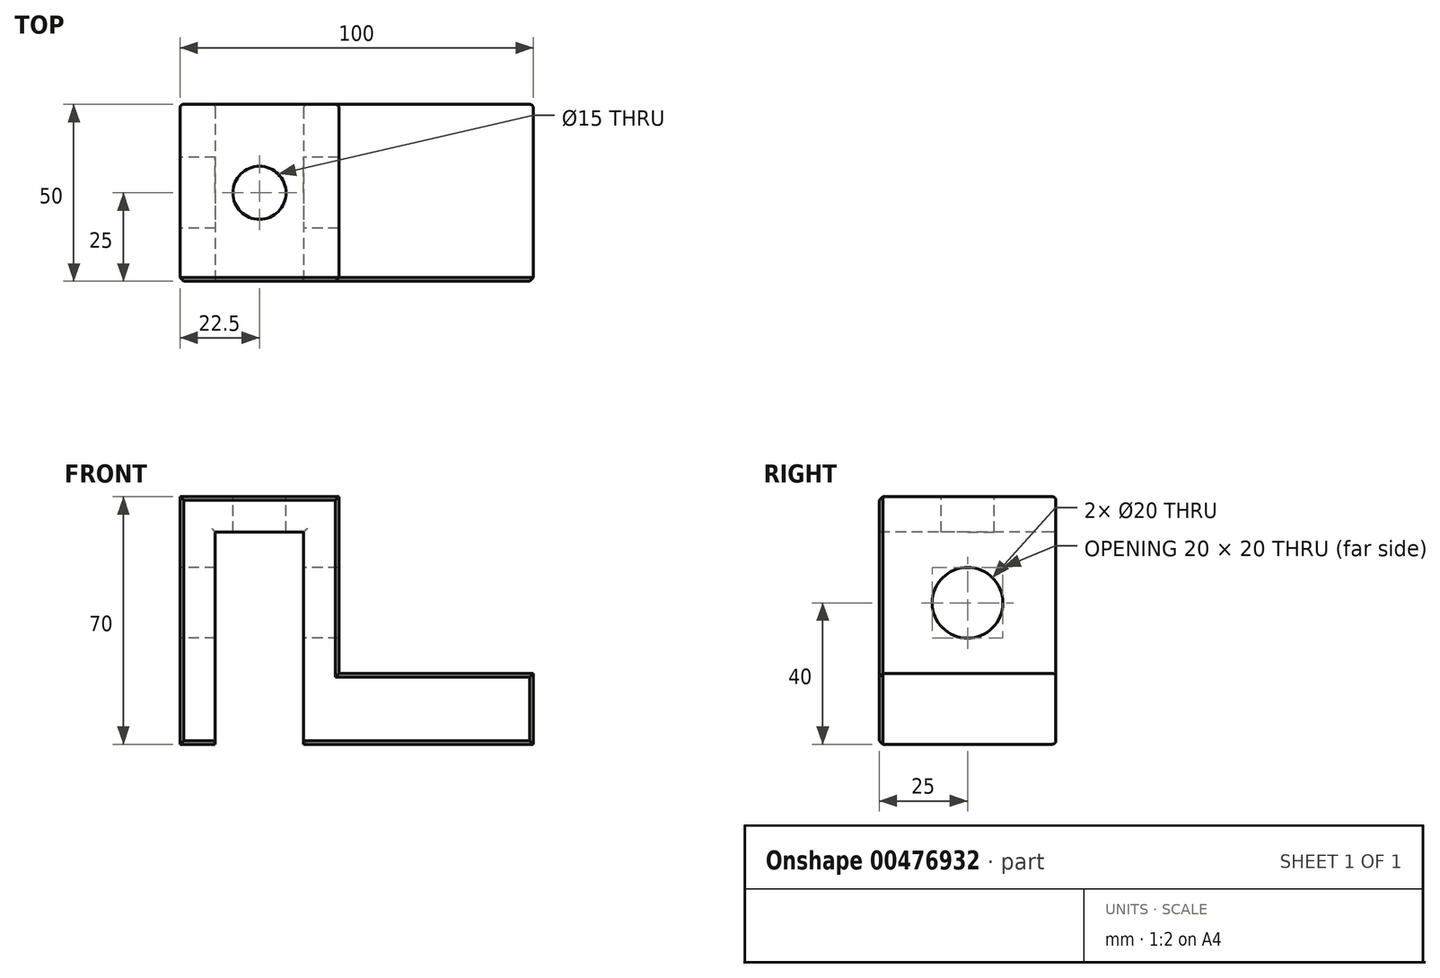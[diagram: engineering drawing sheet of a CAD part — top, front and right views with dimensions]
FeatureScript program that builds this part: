
annotation { "Feature Type Name" : "Feature", "Feature Type Description" : "" }
export const myFeature = defineFeature(function(context is Context, id is Id, definition is map)
    precondition{}
    {
        {
            var Q0;
            Q0=qCreatedBy(makeId("Top.planeOp"),FACE);
            var sketch = newSketch(context, id + "F0", { "sketchPlane" : qUnion([Q0])});
            skLineSegment(sketch, "E0.bottom", {"start": v(0, 0) * mm, "end": v(100, 0) * mm});
            skLineSegment(sketch, "E0.top", {"start": v(0, 50) * mm, "end": v(100, 50) * mm});
            skLineSegment(sketch, "E0.left", {"start": v(0, 0) * mm, "end": v(0, 50) * mm});
            skLineSegment(sketch, "E0.right", {"start": v(100, 0) * mm, "end": v(100, 50) * mm});
            skSolve(sketch);
        }
        {
            var Q0;
            Q0 = qSketchRegion(id + "F0", true);
            extrude(context, id + "F1", {"entities" : qUnion([Q0]), "depth" : 20 * mm});
        }
        {
            var Q0;
            Q0=makeQuery(id+"F1.opExtrude","CAP_FACE",FACE,{"disambiguationData":[OSD([sQuery(id+"F0.wireOp",EDGE,"E0.bottom"),sQuery(id+"F0.wireOp",EDGE,"E0.top"),sQuery(id+"F0.wireOp",EDGE,"E0.left"),sQuery(id+"F0.wireOp",EDGE,"E0.right")])],"isStart":false});
            var sketch = newSketch(context, id + "F2", { "sketchPlane" : qUnion([Q0])});
            skLineSegment(sketch, "E1.bottom", {"start": v(0, 0) * mm, "end": v(45, 0) * mm});
            skLineSegment(sketch, "E1.top", {"start": v(0, 50) * mm, "end": v(45, 50) * mm});
            skLineSegment(sketch, "E1.left", {"start": v(0, 0) * mm, "end": v(0, 50) * mm});
            skLineSegment(sketch, "E1.right", {"start": v(45, 0) * mm, "end": v(45, 50) * mm});
            skSolve(sketch);
        }
        {
            var Q0;
            Q0 = qSketchRegion(id + "F2", true);
            extrude(context, id + "F3", {"entities" : qUnion([Q0]), "operationType" : NewBodyOperationType.ADD, "depth" : 50 * mm});
        }
        {
            var Q0;
            Q0=makeQuery(id+"F3.boolean.opBoolean","MERGE",FACE,{"derivedFrom":[makeQuery(id+"F1.opExtrude","SWEPT_FACE",FACE,{"disambiguationData":[OSD([sQuery(id+"F0.wireOp",EDGE,"E0.bottom")])]}),makeQuery(id+"F3.opExtrude","SWEPT_FACE",FACE,{"disambiguationData":[OSD([sQuery(id+"F2.wireOp",EDGE,"E1.bottom")])]})]});
            var sketch = newSketch(context, id + "F4", { "sketchPlane" : qUnion([Q0])});
            skLineSegment(sketch, "E2.bottom", {"start": v(10, 0) * mm, "end": v(35, 0) * mm});
            skLineSegment(sketch, "E2.top", {"start": v(10, 60) * mm, "end": v(35, 60) * mm});
            skLineSegment(sketch, "E2.left", {"start": v(10, 0) * mm, "end": v(10, 60) * mm});
            skLineSegment(sketch, "E2.right", {"start": v(35, 0) * mm, "end": v(35, 60) * mm});
            skSolve(sketch);
        }
        {
            var Q0;
            Q0 = qSketchRegion(id + "F4", true);
            extrude(context, id + "F5", {"entities" : qUnion([Q0]), "operationType" : NewBodyOperationType.REMOVE, "endBound" : BoundingType.THROUGH_ALL, "oppositeDirection" : true, "depth" : 25 * mm});
        }
        {
            var Q0;
            Q0=makeQuery(id+"F3.boolean.opBoolean","MERGE",FACE,{"derivedFrom":[makeQuery(id+"F1.opExtrude","SWEPT_FACE",FACE,{"disambiguationData":[OSD([sQuery(id+"F0.wireOp",EDGE,"E0.left")])]}),makeQuery(id+"F3.opExtrude","SWEPT_FACE",FACE,{"disambiguationData":[OSD([sQuery(id+"F2.wireOp",EDGE,"E1.left")])]})]});
            var sketch = newSketch(context, id + "F6", { "sketchPlane" : qUnion([Q0])});
            skCircle(sketch, "E3", {"center": v(-25, 40) * mm, "radius": 10 * mm});
            skSolve(sketch);
        }
        {
            var Q0;
            Q0 = qSketchRegion(id + "F6", true);
            var Q1;
            Q1=makeQuery(id+"F5.boolean.opBoolean","COPY",FACE,{"derivedFrom":makeQuery(id+"F5.opExtrude","SWEPT_FACE",FACE,{"disambiguationData":[OSD([sQuery(id+"F4.wireOp",EDGE,"E2.left")])]})});
            extrude(context, id + "F7", {"entities" : qUnion([Q0]), "operationType" : NewBodyOperationType.REMOVE, "endBound" : BoundingType.THROUGH_ALL, "oppositeDirection" : true, "endBoundEntityFace" : qUnion([Q1]), "depth" : 25 * mm});
        }
        {
            var Q0;
            Q0=makeQuery(id+"F3.opExtrude","CAP_FACE",FACE,{"disambiguationData":[OSD([sQuery(id+"F2.wireOp",EDGE,"E1.bottom"),sQuery(id+"F2.wireOp",EDGE,"E1.top"),sQuery(id+"F2.wireOp",EDGE,"E1.left"),sQuery(id+"F2.wireOp",EDGE,"E1.right")])],"isStart":false});
            var sketch = newSketch(context, id + "F8", { "sketchPlane" : qUnion([Q0])});
            skLineSegment(sketch, "E4", {"start": v(45, 0) * mm, "end": v(0, 50) * mm, "construction": true});
            skLineSegment(sketch, "E5", {"start": v(45, 50) * mm, "end": v(0, 0) * mm, "construction": true});
            skCircle(sketch, "E6", {"center": v(22.5, 25) * mm, "radius": 7.5 * mm});
            skSolve(sketch);
        }
        {
            var Q0;
            Q0 = qSketchRegion(id + "F8", true);
            extrude(context, id + "F9", {"entities" : qUnion([Q0]), "operationType" : NewBodyOperationType.REMOVE, "endBound" : BoundingType.UP_TO_NEXT, "oppositeDirection" : true, "depth" : 25 * mm});
        }
        {
            var Q0;
            {var subQ0=sQuery(id+"F0.wireOp",EDGE,"E0.left");var subQ1=sQuery(id+"F0.wireOp",EDGE,"E0.bottom");Q0=makeQuery(id+"F5.boolean.opBoolean","SPLIT",EDGE,{"disambiguationData":[TD([makeQuery(id+"F1.opExtrude","SWEPT_FACE",FACE,{"disambiguationData":[OSD([subQ0])]})])],"derivedFrom":makeQuery(id+"F1.opExtrude","CAP_EDGE",EDGE,{"disambiguationData":[OSD([subQ1])],"isStart":true})});}
            var Q1;
            Q1=makeQuery(id+"F3.boolean.opBoolean","MERGE",EDGE,{"derivedFrom":[makeQuery(id+"F1.opExtrude","SWEPT_EDGE",EDGE,{"disambiguationData":[OSD([sQuery(id+"F0.wireOp",EDGE,"E0.bottom"),sQuery(id+"F0.wireOp",EDGE,"E0.left")])]}),makeQuery(id+"F3.opExtrude","SWEPT_EDGE",EDGE,{"disambiguationData":[OSD([sQuery(id+"F2.wireOp",EDGE,"E1.bottom"),sQuery(id+"F2.wireOp",EDGE,"E1.left")])]})]});
            var Q2;
            Q2=makeQuery(id+"F3.opExtrude","SWEPT_EDGE",EDGE,{"disambiguationData":[OSD([sQuery(id+"F0.wireOp",EDGE,"E0.bottom"),sQuery(id+"F2.wireOp",EDGE,"E1.bottom"),sQuery(id+"F2.wireOp",EDGE,"E1.right")])]});
            var Q3;
            Q3=makeQuery(id+"F3.opExtrude","CAP_EDGE",EDGE,{"disambiguationData":[OSD([sQuery(id+"F2.wireOp",EDGE,"E1.bottom")])],"isStart":false});
            var Q4;
            Q4=makeQuery(id+"F5.boolean.opBoolean","COPY",EDGE,{"derivedFrom":makeQuery(id+"F5.opExtrude","CAP_EDGE",EDGE,{"disambiguationData":[OSD([sQuery(id+"F4.wireOp",EDGE,"E2.left")])],"isStart":true})});
            var Q5;
            Q5=makeQuery(id+"F5.boolean.opBoolean","COPY",EDGE,{"derivedFrom":makeQuery(id+"F5.opExtrude","CAP_EDGE",EDGE,{"disambiguationData":[OSD([sQuery(id+"F4.wireOp",EDGE,"E2.top")])],"isStart":true})});
            var Q6;
            Q6=makeQuery(id+"F5.boolean.opBoolean","COPY",EDGE,{"derivedFrom":makeQuery(id+"F5.opExtrude","CAP_EDGE",EDGE,{"disambiguationData":[OSD([sQuery(id+"F4.wireOp",EDGE,"E2.right")])],"isStart":true})});
            var Q7;
            {var subQ0=sQuery(id+"F0.wireOp",EDGE,"E0.right");var subQ1=sQuery(id+"F0.wireOp",EDGE,"E0.bottom");Q7=makeQuery(id+"F5.boolean.opBoolean","SPLIT",EDGE,{"disambiguationData":[TD([makeQuery(id+"F1.opExtrude","SWEPT_FACE",FACE,{"disambiguationData":[OSD([subQ0])]})])],"derivedFrom":makeQuery(id+"F1.opExtrude","CAP_EDGE",EDGE,{"disambiguationData":[OSD([subQ1])],"isStart":true})});}
            var Q8;
            Q8=makeQuery(id+"F1.opExtrude","CAP_EDGE",EDGE,{"disambiguationData":[OSD([sQuery(id+"F0.wireOp",EDGE,"E0.bottom")])],"isStart":false});
            var Q9;
            Q9=makeQuery(id+"F1.opExtrude","SWEPT_EDGE",EDGE,{"disambiguationData":[OSD([sQuery(id+"F0.wireOp",EDGE,"E0.bottom"),sQuery(id+"F0.wireOp",EDGE,"E0.right")])]});
            chamfer(context, id + "F10", {"entities" : qUnion([Q0, Q1, Q2, Q3, Q4, Q5, Q6, Q7, Q8, Q9]), "width" : 1 * mm, "tangentPropagation" : true});
        }
        {
            var Q0;
            Q0=makeQuery(id+"F3.boolean.opBoolean","MERGE",EDGE,{"derivedFrom":[makeQuery(id+"F1.opExtrude","SWEPT_EDGE",EDGE,{"disambiguationData":[OSD([sQuery(id+"F0.wireOp",EDGE,"E0.top"),sQuery(id+"F0.wireOp",EDGE,"E0.left")])]}),makeQuery(id+"F3.opExtrude","SWEPT_EDGE",EDGE,{"disambiguationData":[OSD([sQuery(id+"F2.wireOp",EDGE,"E1.top"),sQuery(id+"F2.wireOp",EDGE,"E1.left")])]})]});
            var Q1;
            Q1=makeQuery(id+"F3.opExtrude","CAP_EDGE",EDGE,{"disambiguationData":[OSD([sQuery(id+"F2.wireOp",EDGE,"E1.top")])],"isStart":false});
            var Q2;
            Q2=makeQuery(id+"F3.opExtrude","SWEPT_EDGE",EDGE,{"disambiguationData":[OSD([sQuery(id+"F0.wireOp",EDGE,"E0.top"),sQuery(id+"F2.wireOp",EDGE,"E1.top"),sQuery(id+"F2.wireOp",EDGE,"E1.right")])]});
            var Q3;
            Q3=makeQuery(id+"F1.opExtrude","CAP_EDGE",EDGE,{"disambiguationData":[OSD([sQuery(id+"F0.wireOp",EDGE,"E0.top")])],"isStart":false});
            var Q4;
            Q4=makeQuery(id+"F1.opExtrude","SWEPT_EDGE",EDGE,{"disambiguationData":[OSD([sQuery(id+"F0.wireOp",EDGE,"E0.top"),sQuery(id+"F0.wireOp",EDGE,"E0.right")])]});
            var Q5;
            {var subQ0=sQuery(id+"F0.wireOp",EDGE,"E0.right");var subQ1=sQuery(id+"F0.wireOp",EDGE,"E0.top");Q5=makeQuery(id+"F5.boolean.opBoolean","SPLIT",EDGE,{"disambiguationData":[TD([makeQuery(id+"F1.opExtrude","SWEPT_FACE",FACE,{"disambiguationData":[OSD([subQ0])]})])],"derivedFrom":makeQuery(id+"F1.opExtrude","CAP_EDGE",EDGE,{"disambiguationData":[OSD([subQ1])],"isStart":true})});}
            var Q6;
            Q6=makeQuery(id+"F5.boolean.opBoolean","INTERSECT",EDGE,{"derivedFrom":[makeQuery(id+"F3.boolean.opBoolean","MERGE",FACE,{"derivedFrom":[makeQuery(id+"F1.opExtrude","SWEPT_FACE",FACE,{"disambiguationData":[OSD([sQuery(id+"F0.wireOp",EDGE,"E0.top")])]}),makeQuery(id+"F3.opExtrude","SWEPT_FACE",FACE,{"disambiguationData":[OSD([sQuery(id+"F2.wireOp",EDGE,"E1.top")])]})]}),makeQuery(id+"F5.opExtrude","SWEPT_FACE",FACE,{"disambiguationData":[OSD([sQuery(id+"F4.wireOp",EDGE,"E2.right")])]})]});
            var Q7;
            Q7=makeQuery(id+"F5.boolean.opBoolean","INTERSECT",EDGE,{"derivedFrom":[makeQuery(id+"F3.boolean.opBoolean","MERGE",FACE,{"derivedFrom":[makeQuery(id+"F1.opExtrude","SWEPT_FACE",FACE,{"disambiguationData":[OSD([sQuery(id+"F0.wireOp",EDGE,"E0.top")])]}),makeQuery(id+"F3.opExtrude","SWEPT_FACE",FACE,{"disambiguationData":[OSD([sQuery(id+"F2.wireOp",EDGE,"E1.top")])]})]}),makeQuery(id+"F5.opExtrude","SWEPT_FACE",FACE,{"disambiguationData":[OSD([sQuery(id+"F4.wireOp",EDGE,"E2.top")])]})]});
            var Q8;
            Q8=makeQuery(id+"F5.boolean.opBoolean","INTERSECT",EDGE,{"derivedFrom":[makeQuery(id+"F3.boolean.opBoolean","MERGE",FACE,{"derivedFrom":[makeQuery(id+"F1.opExtrude","SWEPT_FACE",FACE,{"disambiguationData":[OSD([sQuery(id+"F0.wireOp",EDGE,"E0.top")])]}),makeQuery(id+"F3.opExtrude","SWEPT_FACE",FACE,{"disambiguationData":[OSD([sQuery(id+"F2.wireOp",EDGE,"E1.top")])]})]}),makeQuery(id+"F5.opExtrude","SWEPT_FACE",FACE,{"disambiguationData":[OSD([sQuery(id+"F4.wireOp",EDGE,"E2.left")])]})]});
            var Q9;
            {var subQ0=sQuery(id+"F0.wireOp",EDGE,"E0.left");var subQ1=sQuery(id+"F0.wireOp",EDGE,"E0.top");Q9=makeQuery(id+"F5.boolean.opBoolean","SPLIT",EDGE,{"disambiguationData":[TD([makeQuery(id+"F1.opExtrude","SWEPT_FACE",FACE,{"disambiguationData":[OSD([subQ0])]})])],"derivedFrom":makeQuery(id+"F1.opExtrude","CAP_EDGE",EDGE,{"disambiguationData":[OSD([subQ1])],"isStart":true})});}
            fillet(context, id + "F11", {"entities" : qUnion([Q0, Q1, Q2, Q3, Q4, Q5, Q6, Q7, Q8, Q9]), "radius" : 1 * mm, "tangentPropagation" : true, "allowEdgeOverflow" : false});
        }
    });
